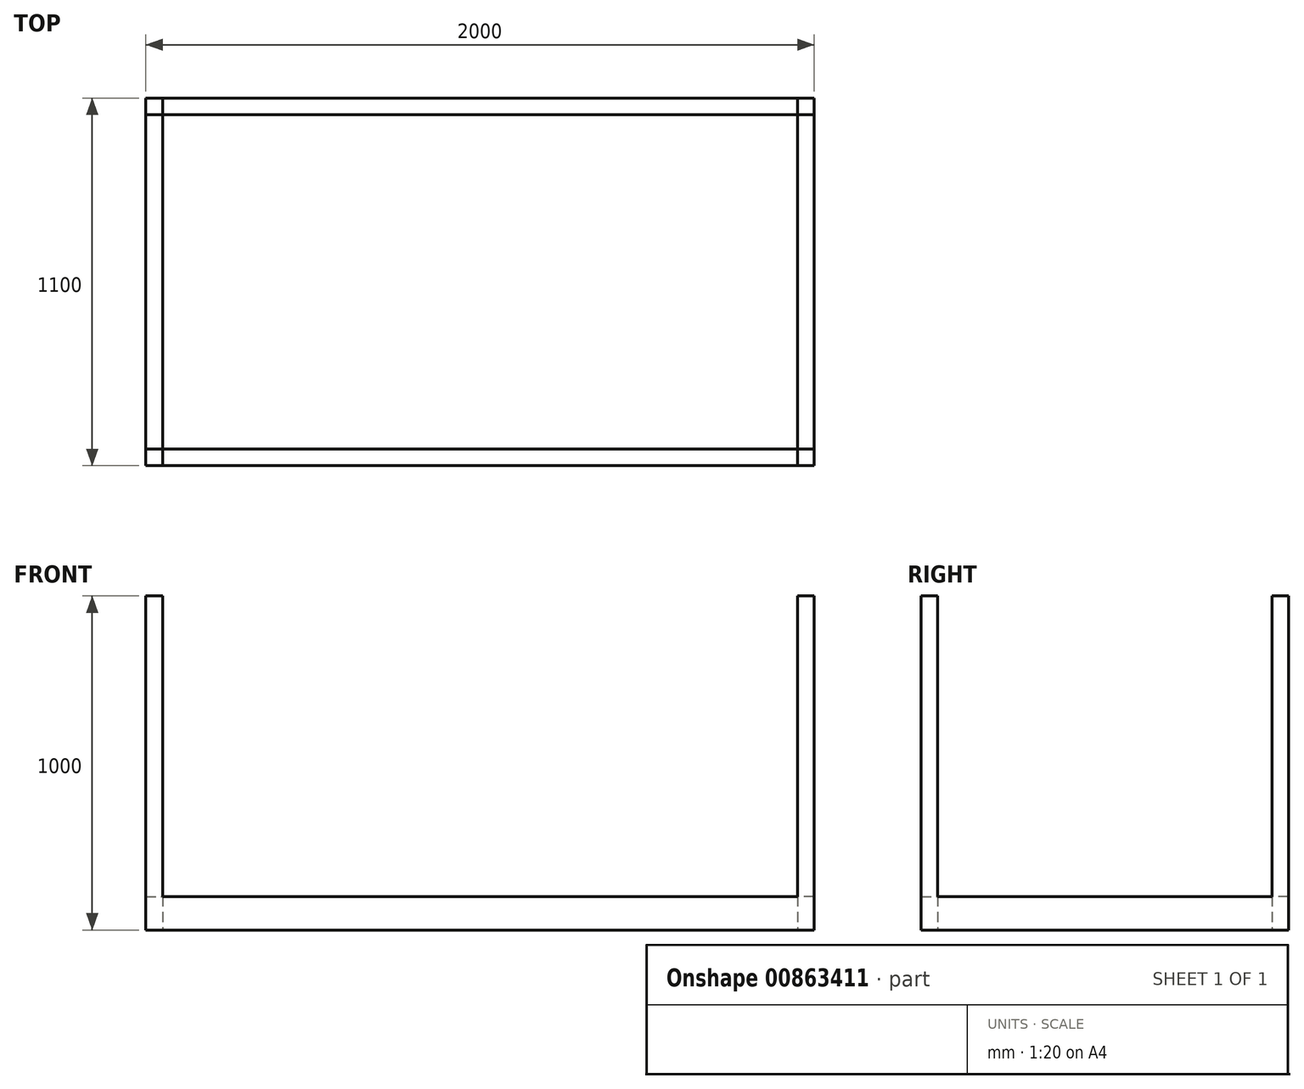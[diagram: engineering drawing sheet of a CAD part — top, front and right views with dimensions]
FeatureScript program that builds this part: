
annotation { "Feature Type Name" : "Feature", "Feature Type Description" : "" }
export const myFeature = defineFeature(function(context is Context, id is Id, definition is map)
    precondition{}
    {
        {
            var Q0;
            Q0=qCreatedBy(makeId("Top.planeOp"),FACE);
            var sketch = newSketch(context, id + "F0", { "sketchPlane" : qUnion([Q0])});
            skLineSegment(sketch, "E0.bottom", {"start": v(-1962.3, 1079.3) * mm, "end": v(37.7, 1079.3) * mm});
            skLineSegment(sketch, "E0.top", {"start": v(-1962.3, -20.7) * mm, "end": v(37.7, -20.7) * mm});
            skLineSegment(sketch, "E0.left", {"start": v(-1962.3, 1079.3) * mm, "end": v(-1962.3, -20.7) * mm});
            skLineSegment(sketch, "E0.right", {"start": v(37.7, 1079.3) * mm, "end": v(37.7, -20.7) * mm});
            skLineSegment(sketch, "E1", {"start": v(-1962.3, -20.7) * mm, "end": v(-1912.3, -20.7) * mm, "construction": true});
            skLineSegment(sketch, "E2", {"start": v(-1912.3, -20.7) * mm, "end": v(-1912.3, 29.3) * mm, "construction": true});
            skLineSegment(sketch, "E3.bottom", {"start": v(-1912.3, 29.3) * mm, "end": v(-12.3, 29.3) * mm});
            skLineSegment(sketch, "E3.top", {"start": v(-1912.3, 1029.3) * mm, "end": v(-12.3, 1029.3) * mm});
            skLineSegment(sketch, "E3.left", {"start": v(-1912.3, 29.3) * mm, "end": v(-1912.3, 1029.3) * mm});
            skLineSegment(sketch, "E3.right", {"start": v(-12.3, 29.3) * mm, "end": v(-12.3, 1029.3) * mm});
            skSolve(sketch);
        }
        {
            var Q0;
            Q0=makeQuery(id+"F0.imprint","IMPRINT",FACE,{"disambiguationData":[TD([[makeQuery(id+"F0.imprint","IMPRINT",EDGE,{"derivedFrom":sQuery(id+"F0.wireOp",EDGE,"E0.bottom")}),-1.0]])]});
            extrude(context, id + "F1", {"entities" : qUnion([Q0]), "depth" : 100 * mm, "offsetDistance" : 25 * mm});
        }
        {
            var Q0;
            Q0=makeQuery(id+"F1.opExtrude","CAP_FACE",FACE,{"disambiguationData":[OSD([sQuery(id+"F0.wireOp",EDGE,"E0.bottom"),sQuery(id+"F0.wireOp",EDGE,"E0.top"),sQuery(id+"F0.wireOp",EDGE,"E0.left"),sQuery(id+"F0.wireOp",EDGE,"E0.right"),sQuery(id+"F0.wireOp",EDGE,"E3.bottom"),sQuery(id+"F0.wireOp",EDGE,"E3.top"),sQuery(id+"F0.wireOp",EDGE,"E3.left"),sQuery(id+"F0.wireOp",EDGE,"E3.right")])],"isStart":false});
            var sketch = newSketch(context, id + "F2", { "sketchPlane" : qUnion([Q0])});
            skLineSegment(sketch, "E4.bottom", {"start": v(-1962.3, 1079.3) * mm, "end": v(-1912.3, 1079.3) * mm});
            skLineSegment(sketch, "E4.top", {"start": v(-1962.3, 1029.3) * mm, "end": v(-1912.3, 1029.3) * mm});
            skLineSegment(sketch, "E4.left", {"start": v(-1962.3, 1079.3) * mm, "end": v(-1962.3, 1029.3) * mm});
            skLineSegment(sketch, "E4.right", {"start": v(-1912.3, 1079.3) * mm, "end": v(-1912.3, 1029.3) * mm});
            skLineSegment(sketch, "E5.bottom", {"start": v(37.7, 1079.3) * mm, "end": v(-12.3, 1079.3) * mm});
            skLineSegment(sketch, "E5.top", {"start": v(37.7, 1029.3) * mm, "end": v(-12.3, 1029.3) * mm});
            skLineSegment(sketch, "E5.left", {"start": v(37.7, 1079.3) * mm, "end": v(37.7, 1029.3) * mm});
            skLineSegment(sketch, "E5.right", {"start": v(-12.3, 1079.3) * mm, "end": v(-12.3, 1029.3) * mm});
            skLineSegment(sketch, "E6.bottom", {"start": v(37.7, -20.7) * mm, "end": v(-12.3, -20.7) * mm});
            skLineSegment(sketch, "E6.top", {"start": v(37.7, 29.3) * mm, "end": v(-12.3, 29.3) * mm});
            skLineSegment(sketch, "E6.left", {"start": v(37.7, -20.7) * mm, "end": v(37.7, 29.3) * mm});
            skLineSegment(sketch, "E6.right", {"start": v(-12.3, -20.7) * mm, "end": v(-12.3, 29.3) * mm});
            skLineSegment(sketch, "E7.bottom", {"start": v(-1962.3, -20.7) * mm, "end": v(-1912.3, -20.7) * mm});
            skLineSegment(sketch, "E7.top", {"start": v(-1962.3, 29.3) * mm, "end": v(-1912.3, 29.3) * mm});
            skLineSegment(sketch, "E7.left", {"start": v(-1962.3, -20.7) * mm, "end": v(-1962.3, 29.3) * mm});
            skLineSegment(sketch, "E7.right", {"start": v(-1912.3, -20.7) * mm, "end": v(-1912.3, 29.3) * mm});
            skSolve(sketch);
        }
        {
            var Q0;
            Q0=makeQuery(id+"F2.imprint","IMPRINT",FACE,{"disambiguationData":[TD([[makeQuery(id+"F2.imprint","IMPRINT",EDGE,{"derivedFrom":sQuery(id+"F2.wireOp",EDGE,"E7.bottom")}),1.0]])]});
            var Q1;
            Q1=makeQuery(id+"F2.imprint","IMPRINT",FACE,{"disambiguationData":[TD([[makeQuery(id+"F2.imprint","IMPRINT",EDGE,{"derivedFrom":sQuery(id+"F2.wireOp",EDGE,"E6.bottom")}),1.0]])]});
            var Q2;
            Q2=makeQuery(id+"F2.imprint","IMPRINT",FACE,{"disambiguationData":[TD([[makeQuery(id+"F2.imprint","IMPRINT",EDGE,{"derivedFrom":sQuery(id+"F2.wireOp",EDGE,"E5.bottom")}),-1.0]])]});
            var Q3;
            Q3=makeQuery(id+"F2.imprint","IMPRINT",FACE,{"disambiguationData":[TD([[makeQuery(id+"F2.imprint","IMPRINT",EDGE,{"derivedFrom":sQuery(id+"F2.wireOp",EDGE,"E4.bottom")}),-1.0]])]});
            extrude(context, id + "F3", {"entities" : qUnion([Q0, Q1, Q2, Q3]), "operationType" : NewBodyOperationType.ADD, "depth" : 900 * mm, "offsetDistance" : 25 * mm});
        }
    });
